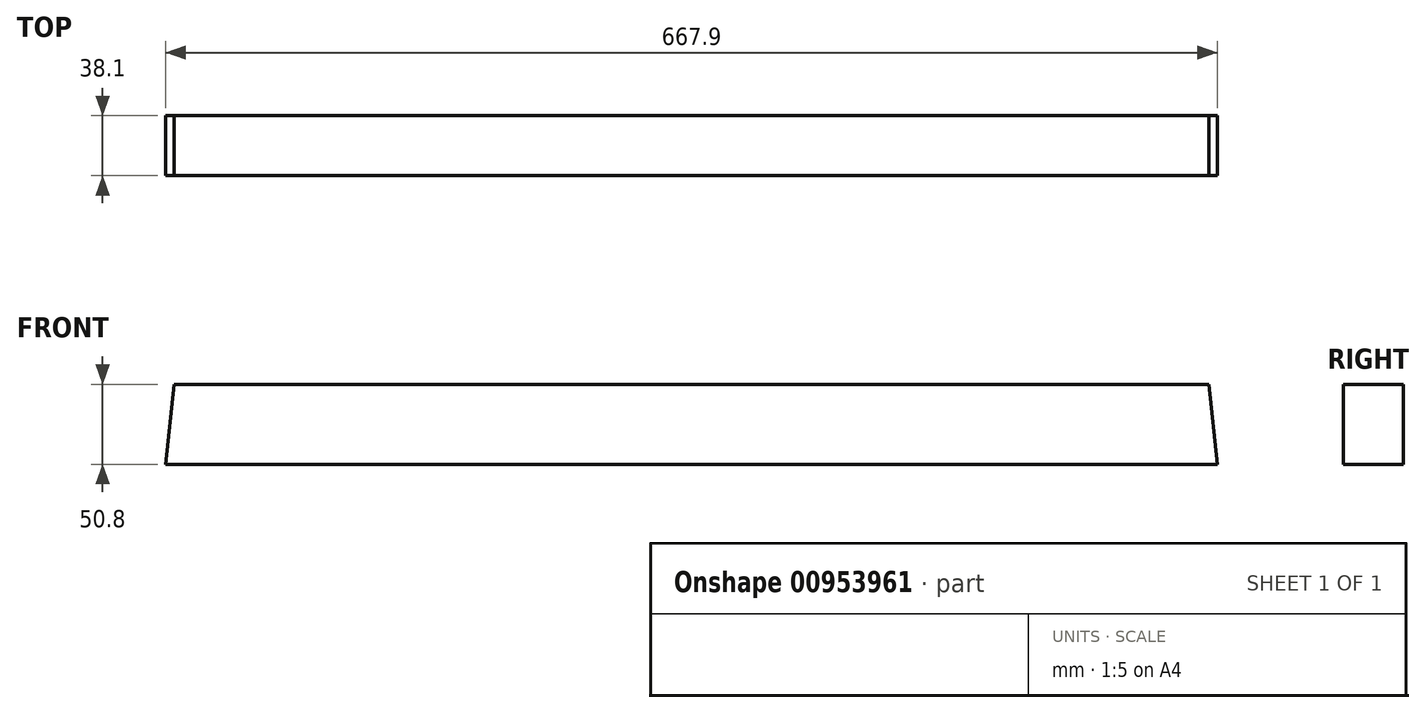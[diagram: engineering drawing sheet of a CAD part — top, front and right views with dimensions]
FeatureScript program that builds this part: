
annotation { "Feature Type Name" : "Feature", "Feature Type Description" : "" }
export const myFeature = defineFeature(function(context is Context, id is Id, definition is map)
    precondition{}
    {
        {
            var Q0;
            Q0=qCreatedBy(makeId("Front.planeOp"),FACE);
            var sketch = newSketch(context, id + "F0", { "sketchPlane" : qUnion([Q0])});
            skLineSegment(sketch, "E0", {"start": v(0, 0) * mm, "end": v(657.23, 0) * mm});
            skLineSegment(sketch, "E1", {"start": v(657.23, 0) * mm, "end": v(662.56, -50.8) * mm});
            skLineSegment(sketch, "E2", {"start": v(662.56, -50.8) * mm, "end": v(-5.34, -50.8) * mm});
            skLineSegment(sketch, "E3", {"start": v(-5.34, -50.8) * mm, "end": v(0, 0) * mm});
            skLineSegment(sketch, "E4", {"start": v(0, 0) * mm, "end": v(0, -50.8) * mm, "construction": true});
            skLineSegment(sketch, "E5", {"start": v(657.23, 0) * mm, "end": v(657.23, -50.8) * mm, "construction": true});
            skSolve(sketch);
        }
        {
            var Q0;
            Q0=makeQuery(id+"F0.imprint","IMPRINT",FACE,{"disambiguationData":[TD([[makeQuery(id+"F0.imprint","IMPRINT",EDGE,{"derivedFrom":sQuery(id+"F0.wireOp",EDGE,"E0")}),-1.0]])]});
            extrude(context, id + "F1", {"entities" : qUnion([Q0]), "depth" : 38.1 * mm, "offsetDistance" : 25.4 * mm});
        }
    });
